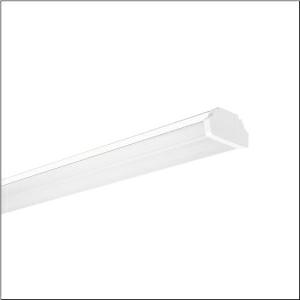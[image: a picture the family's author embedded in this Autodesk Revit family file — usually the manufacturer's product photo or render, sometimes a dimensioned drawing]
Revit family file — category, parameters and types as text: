
# Revit family: modario_31_gen_2_53bm812mv485c2_3aa5
name_source: partatom
category: Lighting Fixtures
units: mm (PartAtom-declared; Revit-internal decimal feet)

## family parameters
Cut with Voids When Loaded = No
Host = Face
Light Source = No
Part Type = Normal
Room Calculation Point = No
Round Connector Dimension = Use Diameter
Shared = No

## types (1)
- --- (1 x LED, 8950 lm, 48.2 W, 4000K)
    Apparent Load = 48 VA
    CIE Flux Codes = 47 80 95 93 100
    Color Rendering = 80
    Color Temperature = 4000K
    Default Elevation = 1800 mm
    Description = Modario 31 Gen.2, luminaire insert, of sheet steel, coil coated, white, length: 1.495mm, width: 81mm, height: 82mm, 5x system unit, system units: 299mm, LED rated luminous flux: 8.950lm, light colour: 840, SDCM (Standard Deviation of Colour Matching)MacAdam ≤ 3 SDCM (initial), control gear: ON/OFF Multilumen, control gear: ECG, with plug, 3-pole, with phase selection, mains connection: 220..240V, AC, 50/60Hz, rated input power: 48W, through-wiring accessed according to module size, primary optical cover: cover, of PMMA, light emission: direct distribution, primary light characteristic: symmetric, protection rating (complete): IP20, protection rating (LED compartment): IP50, insulation class (complete): insulation class I (protective earthing), certification: CE, ENEC, VDE, UKCA, impact resistance: IK03, permissible ambient temperature for indoor applications: -35..+50°C, corresponds to IFS (International Featured Standards) requirements for safety and quality in the food industry, reducing of maximum allowable ambient temperature of 5°C with ceiling mounting, IP40 when using the optional accessory 5TP9018, packaging unit: 1 piece
    Height = 92 mm
    Lamp = 1 x LED
    Lamp Light Flux = 8950 lm
    Lamp Power = 48.2 W
    Lamp count = 1
    Length = 1495 mm
    Luminous efficacy = 186 lm/W
    Manufacturer = Siteco
    ModVariant = No
    Model = 53BM812MV485C2
    Mounting Place = Ceiling
    Mounting Type = Pendant
    Number of Poles = 1
    OnlyDefault = Yes
    Power Factor = 1
    Product Name = Modario 31 Gen.2
    Product group = luminaire insert | ceiling pendant
    ProductGroupID = 901
    Protection Class = Protection class I
    Protection Degree = IP 20
    RLX_Detail_Level = 1
    RLX_Emergency_Light_Flux = 0 lm
    RLX_Emergency_Type = 0
    RLX_Emergency_Type_DB = No
    RlxData = <blob elided: 39873 chars, md5=68e2dba2>
    Socket = socket
    Standby Power = 0 W
    System Light Flux = 8950 lm
    System Power = 48 W
    Type Comments = factory setting: luminous flux: 100 % | (A | C | E) | 112 mA
    Type Image = l_1341886.jpg
    URL = http://relux.com
    VarID = @adj_042317
    Voltage = 0 V
    Weight = 0.00 kg
    Width = 81 mm

## geometry (parser evidence)
native form markers: Blend x4, Sweep x11
no freeform markers — native parametric forms only
